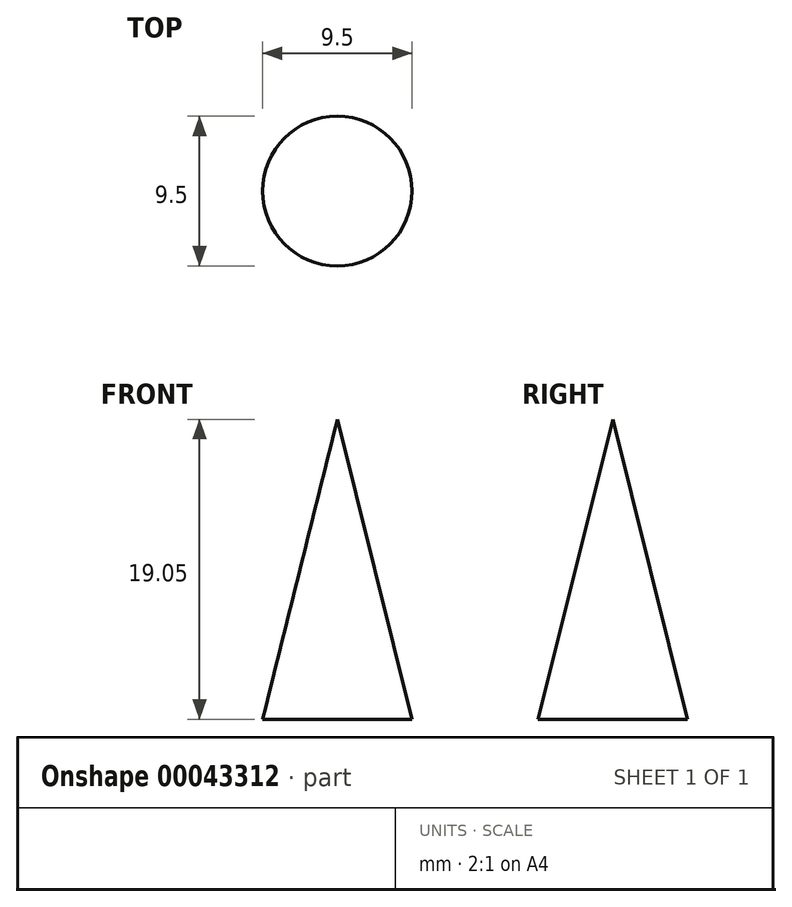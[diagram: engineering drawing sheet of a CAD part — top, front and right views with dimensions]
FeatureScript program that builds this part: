
annotation { "Feature Type Name" : "Feature", "Feature Type Description" : "" }
export const myFeature = defineFeature(function(context is Context, id is Id, definition is map)
    precondition{}
    {
        {
            var Q0;
            Q0=qCreatedBy(makeId("Front.planeOp"),FACE);
            var sketch = newSketch(context, id + "F0", { "sketchPlane" : qUnion([Q0])});
            skLineSegment(sketch, "E0", {"start": v(0, 19.05) * mm, "end": v(0, 0) * mm});
            skLineSegment(sketch, "E1", {"start": v(0, 0) * mm, "end": v(4.75, 0) * mm});
            skLineSegment(sketch, "E2", {"start": v(4.75, 0) * mm, "end": v(0, 19.05) * mm});
            skSolve(sketch);
        }
        {
            var Q0;
            Q0 = qSketchRegion(id + "F0", true);
            var Q1;
            Q1=sQuery(id+"F0.wireOp",EDGE,"E0");
            revolve(context, id + "F1", {"entities" : qUnion([Q0]), "axis" : qUnion([Q1]), "revolveType" : RevolveType.FULL});
        }
    });
